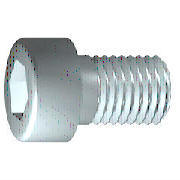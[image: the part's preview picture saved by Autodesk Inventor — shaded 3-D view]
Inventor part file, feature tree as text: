
AUTODESK INVENTOR PART (.ipt)
format: ipt  version: 2021.2 (Build 252289000, 289)  size: 184,320 bytes
history: native  units: mm (DEFAULTED — no unit token found)
features: sketch x2, other x1, extrude x1, plane x1, fillet x1
ambient origin geometry x7: Origin, YZ Plane, XY Plane, X Axis, Y Axis, Z Axis, Center Point
bodies: Solid1 (feature_tree)
feature tree (6):
  other  "Базовый элемент"
  extrude  "Паз"  Depth=20.0mm
  plane  "Work Plane1"
  fillet  "Fillet2"  Radius=0.429515mm
  sketch  "Эскиз1"
  sketch  "Эскиз2"
